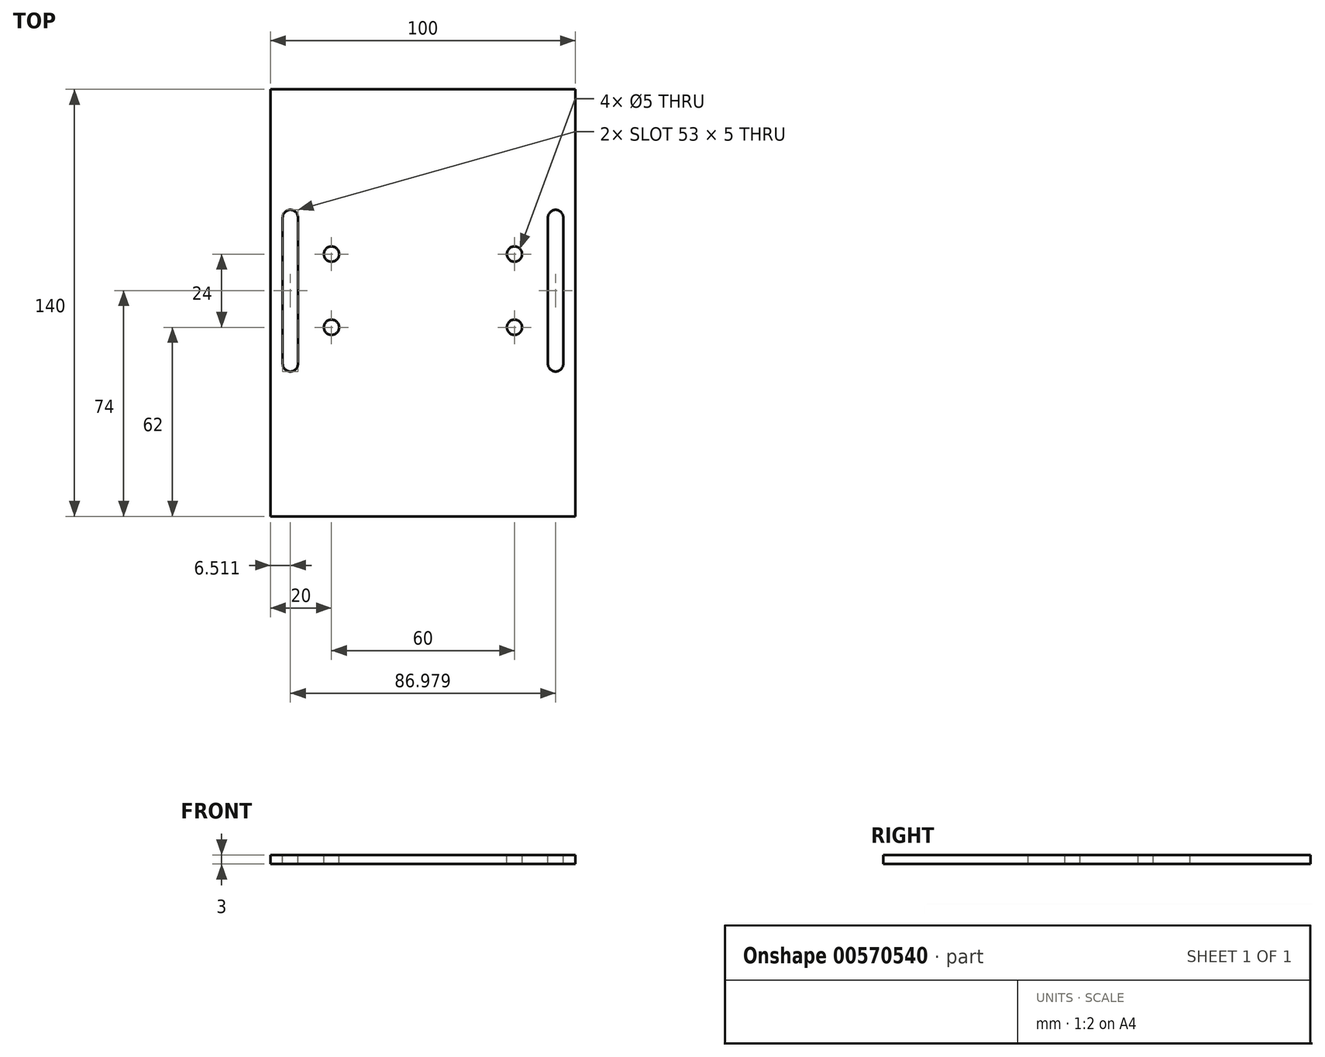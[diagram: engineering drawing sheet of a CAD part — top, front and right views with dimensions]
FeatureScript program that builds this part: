
annotation { "Feature Type Name" : "Feature", "Feature Type Description" : "" }
export const myFeature = defineFeature(function(context is Context, id is Id, definition is map)
    precondition{}
    {
        {
            var Q0;
            Q0=qCreatedBy(makeId("Top.planeOp"),FACE);
            var sketch = newSketch(context, id + "F0", { "sketchPlane" : qUnion([Q0])});
            skLineSegment(sketch, "E0.bottom", {"start": v(0, 0) * mm, "end": v(50, 0) * mm});
            skLineSegment(sketch, "E0.top", {"start": v(0, 140) * mm, "end": v(50, 140) * mm});
            skLineSegment(sketch, "E0.left", {"start": v(0, 0) * mm, "end": v(0, 140) * mm});
            skLineSegment(sketch, "E0.right", {"start": v(50, 0) * mm, "end": v(50, 140) * mm});
            skSolve(sketch);
        }
        {
            var Q0;
            Q0=makeQuery(id+"F0.imprint","IMPRINT",FACE,{"disambiguationData":[TD([[makeQuery(id+"F0.imprint","IMPRINT",EDGE,{"derivedFrom":sQuery(id+"F0.wireOp",EDGE,"E0.bottom")}),1.0]])]});
            extrude(context, id + "F1", {"entities" : qUnion([Q0]), "oppositeDirection" : true, "depth" : 3 * mm, "offsetDistance" : 25 * mm});
        }
        {
            var Q0;
            Q0=makeQuery(id+"F1.opExtrude","CAP_FACE",FACE,{"disambiguationData":[OSD([sQuery(id+"F0.wireOp",EDGE,"E0.bottom"),sQuery(id+"F0.wireOp",EDGE,"E0.top"),sQuery(id+"F0.wireOp",EDGE,"E0.left"),sQuery(id+"F0.wireOp",EDGE,"E0.right")])],"isStart":true});
            var sketch = newSketch(context, id + "F2", { "sketchPlane" : qUnion([Q0])});
            skLineSegment(sketch, "E1", {"start": v(30, 62) * mm, "end": v(30, 86) * mm});
            skSolve(sketch);
        }
        {
            var Q0;
            Q0=sQuery(id+"F2.wireOp",VERTEX,"E1.end");
            var Q1;
            Q1=sQuery(id+"F2.wireOp",VERTEX,"E1.start");
            var Q2;
            Q2=makeQuery(id+"F1.opExtrude","SWEPT_BODY",BODY,{"disambiguationData":[OSD([sQuery(id+"F0.wireOp",EDGE,"E0.bottom"),sQuery(id+"F0.wireOp",EDGE,"E0.top"),sQuery(id+"F0.wireOp",EDGE,"E0.left"),sQuery(id+"F0.wireOp",EDGE,"E0.right")])]});
            hole(context, id + "F3", {"style" : HoleStyle.SIMPLE, "endStyle" : HoleEndStyle.THROUGH, "holeDiameter" : 5 * mm, "isTappedThrough" : true, "tappedDepth" : 12 * mm, "tapClearance" : 3, "locations" : qUnion([Q0, Q1]), "scope" : qUnion([Q2])});
        }
        {
            var Q0;
            Q0=makeQuery(id+"F1.opExtrude","CAP_FACE",FACE,{"disambiguationData":[OSD([sQuery(id+"F0.wireOp",EDGE,"E0.bottom"),sQuery(id+"F0.wireOp",EDGE,"E0.top"),sQuery(id+"F0.wireOp",EDGE,"E0.left"),sQuery(id+"F0.wireOp",EDGE,"E0.right")])],"isStart":true});
            var sketch = newSketch(context, id + "F4", { "sketchPlane" : qUnion([Q0])});
            skLineSegment(sketch, "E2", {"start": v(43.49, 50) * mm, "end": v(43.49, 98) * mm});
            skArc(sketch, "E3.0.startCap", {"start": v(45.99, 50) * mm, "mid": v(43.49, 47.5) * mm, "end": v(40.99, 50) * mm});
            skArc(sketch, "E3.0.endCap", {"start": v(40.99, 98) * mm, "mid": v(43.49, 100.5) * mm, "end": v(45.99, 98) * mm});
            skLineSegment(sketch, "E3.0.left", {"start": v(40.99, 50) * mm, "end": v(40.99, 98) * mm});
            skLineSegment(sketch, "E3.0.right", {"start": v(45.99, 50) * mm, "end": v(45.99, 98) * mm});
            skSolve(sketch);
        }
        {
            var Q0;
            Q0 = qSketchRegion(id + "F4", true);
            extrude(context, id + "F5", {"entities" : qUnion([Q0]), "operationType" : NewBodyOperationType.REMOVE, "oppositeDirection" : true, "depth" : 39.83 * mm, "offsetDistance" : 25 * mm});
        }
        {
            var Q0;
            Q0=makeQuery(id+"F1.opExtrude","SWEPT_BODY",BODY,{"disambiguationData":[OSD([sQuery(id+"F0.wireOp",EDGE,"E0.bottom"),sQuery(id+"F0.wireOp",EDGE,"E0.top"),sQuery(id+"F0.wireOp",EDGE,"E0.left"),sQuery(id+"F0.wireOp",EDGE,"E0.right")])]});
            var Q1;
            Q1=qCreatedBy(makeId("Right.planeOp"),FACE);
            mirror(context, id + "F6", {"operationType" : NewBodyOperationType.ADD, "entities" : qUnion([Q0]), "mirrorPlane" : qUnion([Q1])});
        }
    });
